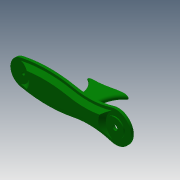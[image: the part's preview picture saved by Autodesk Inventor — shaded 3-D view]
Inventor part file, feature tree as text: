
AUTODESK INVENTOR PART (.ipt)
format: ipt  version: 2013 (Build 170138000, 138)  size: 411,648 bytes
history: native  units: mm
features: extrude x15, sketch x15, chamfer x2, fillet x1
ambient origin geometry x8: Origin, YZ Plane, XZ Plane, XY Plane, X Axis, Y Axis, Z Axis, Center Point
bodies: Solid1 (feature_tree)
feature tree (33):
  extrude  "Extrusion1"  Depth=50.0mm
  extrude  "Extrusion2"  Depth=15.0mm
  extrude  "Extrusion3"  Depth=5.0mm TaperAngle=0.0deg
  extrude  "Extrusion4"  Depth=18.1mm
  extrude  "Extrusion5"  Depth=20.0mm
  extrude  "Extrusion6"  Depth=9.5mm
  sketch  "Sketch7"  dims[d15=9.9mm d16=9.5mm]
  extrude  "Extrusion7"  Depth=9.5mm
  chamfer  "Chamfer1"  Distance=5.0mm
  extrude  "Extrusion8"  Depth=2.0mm
  extrude  "Extrusion17"  Depth=5.0mm TaperAngle=0.0deg
  chamfer  "Chamfer2"  Distance=5.0mm
  extrude  "Extrusion25"  Depth=5.0mm TaperAngle=0.0deg
  extrude  "Extrusion26"  Depth=20.0mm
  extrude  "Extrusion27"  Depth=30.0mm
  sketch  "Sketch30"  dims[d26=2.0mm d29=2.0mm]
  extrude  "Extrusion28"  Depth=7.3mm TaperAngle=0.0deg
  extrude  "Extrusion30"  Depth=7.3mm TaperAngle=45.0deg
  extrude  "Extrusion31"  Depth=12.3mm TaperAngle=0.0deg
  fillet  "Fillet3"  Radius=6.0mm
  sketch  "Sketch1"  dims[d0=180.0mm d1=50.0mm]
  sketch  "Sketch2"  dims[d2=5.0mm d3=0.0mm d4=15.0mm]
  sketch  "Sketch3"  dims[d5=15.0mm d6=5.0mm d7=0.0mm]
  sketch  "Sketch4"  dims[d9=34.65mm d10=18.1mm]
  sketch  "Sketch5"  dims[d11=55.0mm d12=20.0mm]
  sketch  "Sketch6"  dims[d13=40.2mm d14=9.5mm]
  sketch  "Sketch8"  dims[d17=9.9mm]
  sketch  "Sketch9"  dims[d18=3.0mm]
  sketch  "Sketch18"  dims[d19=3.0mm]
  sketch  "Sketch27"  dims[d20=3.0mm]
  sketch  "Sketch28"  dims[d21=3.0mm]
  sketch  "Sketch29"  dims[d22=13.6mm d23=5.0mm d24=0.0mm]
  sketch  "Sketch32"  dims[d30=2.0mm d31=5.0mm d32=0.0mm d63=5.0mm d64=0.0mm d65=5.0mm d66=0.0mm d72=20.0mm d73=30.0mm d74=7.3mm d75=0.0mm d76=7.3mm d77=2.0mm d78=45.0deg d79=12.3mm d80=0.0mm d114=6.0mm d115=5.0mm d116=0.0mm d117=7.3mm d118=2.0mm d119=45.0deg d155=35.0mm d156=2.0mm d157=0.0mm d158=10.0mm d159=2.0mm d160=0.0mm d161=5.0mm d162=0.0mm d177=72.6mm d178=0.0mm d183=20.0mm d184=80.0mm d185=42.0mm d186=42.0mm d187=20.0mm d188=0.0mm d189=72.6mm d190=0.0mm d191=4.988mm]
